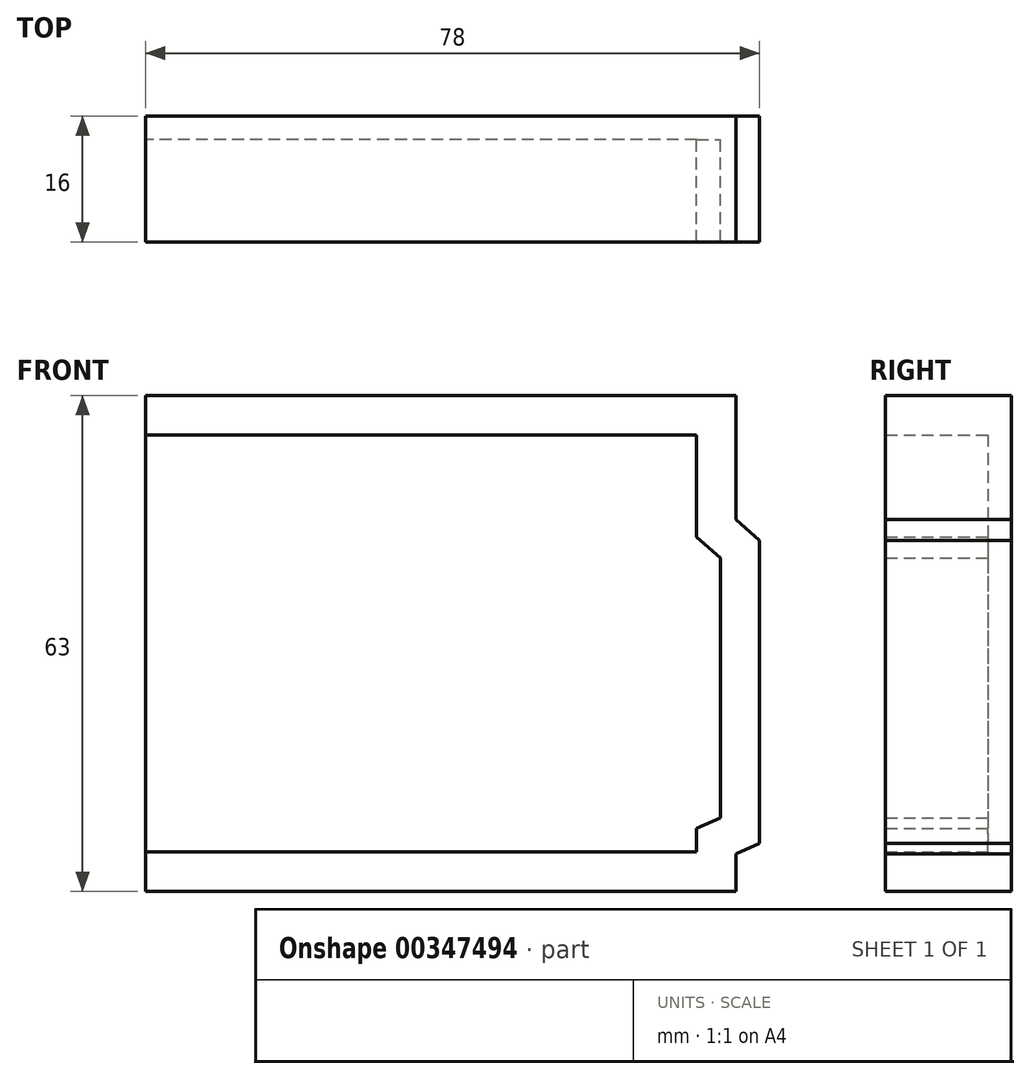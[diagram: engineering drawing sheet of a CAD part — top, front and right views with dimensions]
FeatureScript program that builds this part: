
annotation { "Feature Type Name" : "Feature", "Feature Type Description" : "" }
export const myFeature = defineFeature(function(context is Context, id is Id, definition is map)
    precondition{}
    {
        {
            var Q0;
            Q0=qCreatedBy(makeId("Front.planeOp"),FACE);
            var sketch = newSketch(context, id + "F0", { "sketchPlane" : qUnion([Q0])});
            skLineSegment(sketch, "E0", {"start": v(0, 0) * mm, "end": v(0, -53) * mm});
            skLineSegment(sketch, "E1", {"start": v(0, -53) * mm, "end": v(65, -53) * mm});
            skLineSegment(sketch, "E2", {"start": v(65, -53) * mm, "end": v(65, -50) * mm});
            skLineSegment(sketch, "E3", {"start": v(0, 0) * mm, "end": v(65, 0) * mm});
            skLineSegment(sketch, "E4", {"start": v(65, 0) * mm, "end": v(65, -13) * mm});
            skLineSegment(sketch, "E5", {"start": v(65, -13) * mm, "end": v(68, -15.65) * mm});
            skLineSegment(sketch, "E6", {"start": v(68, -15.65) * mm, "end": v(68, -48.65) * mm});
            skLineSegment(sketch, "E7", {"start": v(68, -48.65) * mm, "end": v(65, -50) * mm});
            skLineSegment(sketch, "E8.0", {"start": v(-5, 5) * mm, "end": v(-5, -58) * mm});
            skLineSegment(sketch, "E8.1", {"start": v(-5, 5) * mm, "end": v(70, 5) * mm});
            skLineSegment(sketch, "E8.2", {"start": v(-5, -58) * mm, "end": v(70, -58) * mm});
            skLineSegment(sketch, "E8.3", {"start": v(70, 5) * mm, "end": v(70, -10.74) * mm});
            skLineSegment(sketch, "E8.4", {"start": v(70, -58) * mm, "end": v(70, -53.23) * mm});
            skLineSegment(sketch, "E8.5", {"start": v(73, -51.87) * mm, "end": v(70, -53.23) * mm});
            skLineSegment(sketch, "E8.6", {"start": v(73, -13.39) * mm, "end": v(73, -51.87) * mm});
            skLineSegment(sketch, "E8.7", {"start": v(70, -10.74) * mm, "end": v(73, -13.39) * mm});
            skLineSegment(sketch, "E9", {"start": v(0, 0) * mm, "end": v(-5, 0) * mm});
            skLineSegment(sketch, "E10", {"start": v(0, -53) * mm, "end": v(-5, -53) * mm});
            skSolve(sketch);
        }
        {
            var Q0;
            Q0=makeQuery(id+"F0.imprint","IMPRINT",FACE,{"disambiguationData":[TD([[makeQuery(id+"F0.imprint","IMPRINT",EDGE,{"derivedFrom":sQuery(id+"F0.wireOp",EDGE,"E1")}),-1.0]])]});
            extrude(context, id + "F1", {"entities" : qUnion([Q0]), "depth" : 16 * mm});
        }
        {
            var Q0;
            Q0 = qSketchRegion(id + "F0", true);
            extrude(context, id + "F2", {"entities" : qUnion([Q0]), "operationType" : NewBodyOperationType.ADD, "depth" : 1.7 * mm});
        }
        {
            var Q0;
            Q0 = qSketchRegion(id + "F0", true);
            extrude(context, id + "F3", {"entities" : qUnion([Q0]), "operationType" : NewBodyOperationType.ADD, "depth" : 3 * mm});
        }
        {
            var Q0;
            Q0=makeQuery(id+"F0.imprint","IMPRINT",FACE,{"disambiguationData":[TD([[makeQuery(id+"F0.imprint","IMPRINT",EDGE,{"derivedFrom":sQuery(id+"F0.wireOp",EDGE,"E0")}),1.0]])]});
            extrude(context, id + "F4", {"entities" : qUnion([Q0]), "operationType" : NewBodyOperationType.ADD, "depth" : 3 * mm});
        }
    });
